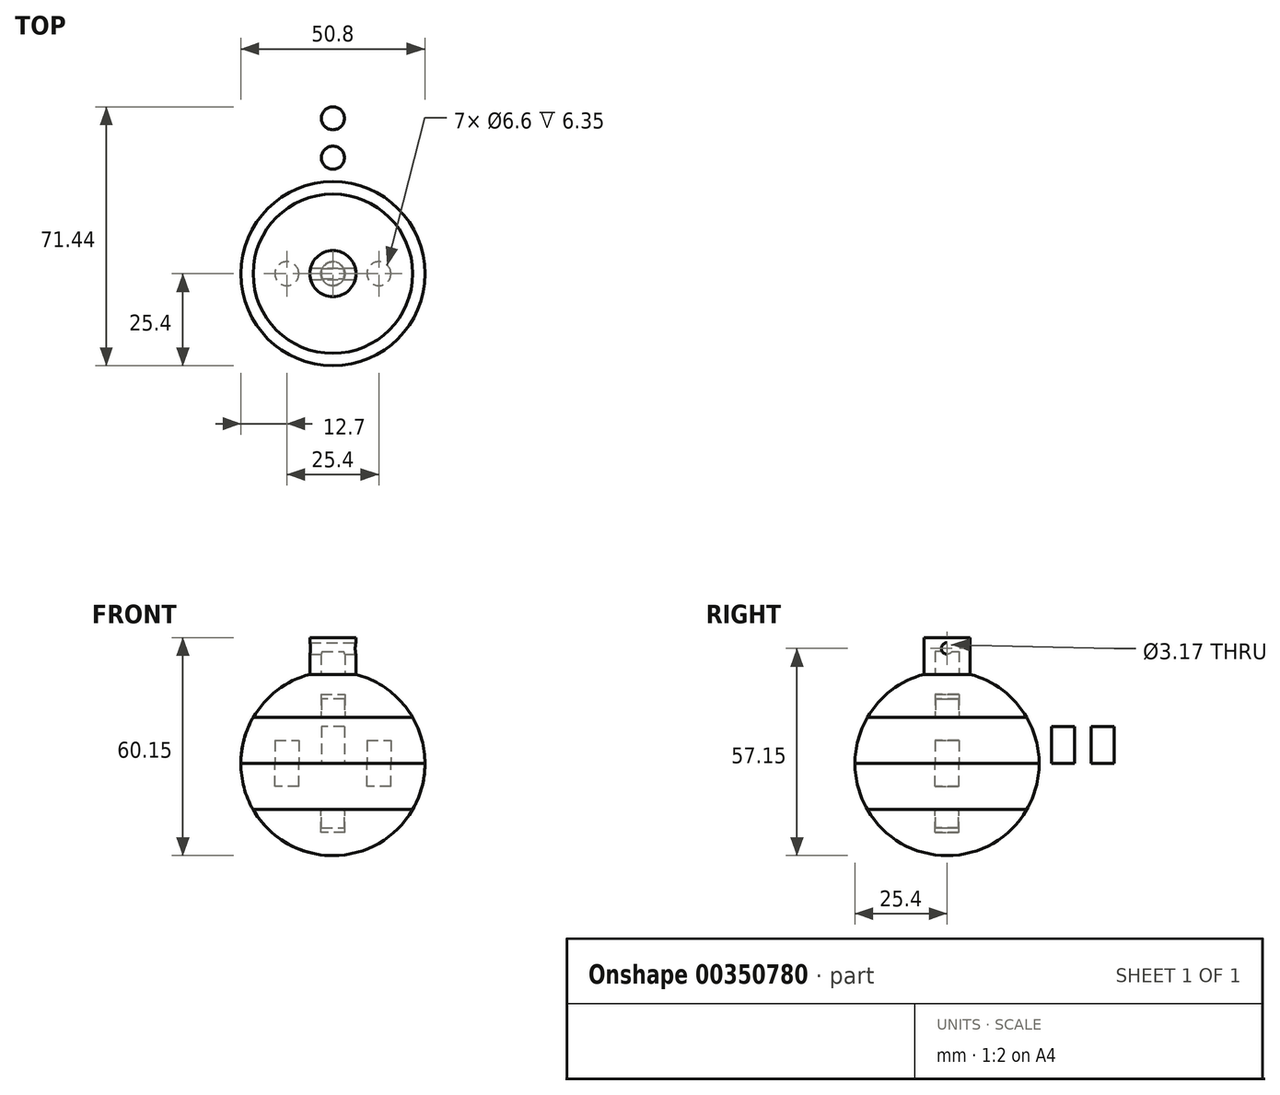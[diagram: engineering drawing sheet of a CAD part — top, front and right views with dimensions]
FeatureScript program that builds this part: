
annotation { "Feature Type Name" : "Feature", "Feature Type Description" : "" }
export const myFeature = defineFeature(function(context is Context, id is Id, definition is map)
    precondition{}
    {
        {
            var Q0;
            Q0=qCreatedBy(makeId("Front.planeOp"),FACE);
            var sketch = newSketch(context, id + "F0", { "sketchPlane" : qUnion([Q0])});
            skArc(sketch, "E0", {"start": v(0, -25.4) * mm, "mid": v(12.7, -22) * mm, "end": v(22, -12.7) * mm});
            skLineSegment(sketch, "E1", {"start": v(0, -25.4) * mm, "end": v(0, -12.7) * mm});
            skLineSegment(sketch, "E2", {"start": v(0, -12.7) * mm, "end": v(22, -12.7) * mm});
            skSolve(sketch);
        }
        {
            var Q0;
            Q0 = qSketchRegion(id + "F0", true);
            var Q1;
            Q1=sQuery(id+"F0.wireOp",EDGE,"E1");
            revolve(context, id + "F1", {"entities" : qUnion([Q0]), "axis" : qUnion([Q1]), "revolveType" : RevolveType.FULL});
        }
        {
            var Q0;
            Q0=qCreatedBy(makeId("Front.planeOp"),FACE);
            var sketch = newSketch(context, id + "F2", { "sketchPlane" : qUnion([Q0])});
            skArc(sketch, "E3", {"start": v(22, -12.7) * mm, "mid": v(24.53, -6.57) * mm, "end": v(25.4, 0) * mm});
            skLineSegment(sketch, "E4", {"start": v(0, 0) * mm, "end": v(25.4, 0) * mm});
            skLineSegment(sketch, "E5", {"start": v(0, 0) * mm, "end": v(0, -12.7) * mm});
            skLineSegment(sketch, "E6", {"start": v(0, -12.7) * mm, "end": v(22, -12.7) * mm});
            skSolve(sketch);
        }
        {
            var Q0;
            Q0 = qSketchRegion(id + "F2", true);
            var Q1;
            Q1=sQuery(id+"F2.wireOp",EDGE,"E5");
            revolve(context, id + "F3", {"entities" : qUnion([Q0]), "axis" : qUnion([Q1]), "revolveType" : RevolveType.FULL});
        }
        {
            var Q0;
            Q0=qCreatedBy(makeId("Front.planeOp"),FACE);
            var sketch = newSketch(context, id + "F4", { "sketchPlane" : qUnion([Q0])});
            skArc(sketch, "E7", {"start": v(25.4, 0) * mm, "mid": v(24.53, 6.57) * mm, "end": v(22, 12.7) * mm});
            skLineSegment(sketch, "E8", {"start": v(0, 0) * mm, "end": v(25.4, 0) * mm});
            skLineSegment(sketch, "E9", {"start": v(0, 0) * mm, "end": v(0, 12.7) * mm});
            skLineSegment(sketch, "E10", {"start": v(0, 12.7) * mm, "end": v(22, 12.7) * mm});
            skSolve(sketch);
        }
        {
            var Q0;
            Q0=makeQuery(id+"F4.imprint","IMPRINT",FACE,{"disambiguationData":[TD([[makeQuery(id+"F4.imprint","IMPRINT",EDGE,{"derivedFrom":sQuery(id+"F4.wireOp",EDGE,"E7")}),1.0]])]});
            var Q1;
            Q1=sQuery(id+"F4.wireOp",EDGE,"E9");
            revolve(context, id + "F5", {"entities" : qUnion([Q0]), "axis" : qUnion([Q1]), "revolveType" : RevolveType.FULL});
        }
        {
            var Q0;
            Q0=qCreatedBy(makeId("Front.planeOp"),FACE);
            var sketch = newSketch(context, id + "F6", { "sketchPlane" : qUnion([Q0])});
            skArc(sketch, "E11", {"start": v(22, 12.7) * mm, "mid": v(15.37, 20.22) * mm, "end": v(6.35, 24.6) * mm});
            skLineSegment(sketch, "E12", {"start": v(0, 24.6) * mm, "end": v(0, 12.7) * mm});
            skLineSegment(sketch, "E13", {"start": v(0, 12.7) * mm, "end": v(22, 12.7) * mm});
            skLineSegment(sketch, "E14", {"start": v(0, 24.6) * mm, "end": v(6.35, 24.6) * mm});
            skPoint(sketch, "E15.orphan", {"position": v(0, 25.4) * mm});
            skSolve(sketch);
        }
        {
            var Q0;
            Q0 = qSketchRegion(id + "F6", true);
            var Q1;
            Q1=sQuery(id+"F6.wireOp",EDGE,"E12");
            revolve(context, id + "F7", {"entities" : qUnion([Q0]), "axis" : qUnion([Q1]), "revolveType" : RevolveType.FULL});
        }
        {
            var Q0;
            Q0=makeQuery(id+"F7.opRevolve","SWEPT_FACE",FACE,{"disambiguationData":[OSD([sQuery(id+"F6.wireOp",EDGE,"E14")])]});
            var sketch = newSketch(context, id + "F8", { "sketchPlane" : qUnion([Q0])});
            skCircle(sketch, "E16", {"center": v(0, 0) * mm, "radius": 3.18 * mm});
            skSolve(sketch);
        }
        {
            var Q0;
            Q0=makeQuery(id+"F8.imprint","IMPRINT",FACE,{"disambiguationData":[TD([[makeQuery(id+"F8.imprint","IMPRINT",EDGE,{"derivedFrom":sQuery(id+"F8.wireOp",EDGE,"E16")}),1.0]])]});
            extrude(context, id + "F9", {"entities" : qUnion([Q0]), "operationType" : NewBodyOperationType.ADD, "depth" : 5.08 * mm});
        }
        {
            var Q0;
            Q0=makeQuery(id+"F7.opRevolve","SWEPT_FACE",FACE,{"disambiguationData":[OSD([sQuery(id+"F6.wireOp",EDGE,"E14")])]});
            var sketch = newSketch(context, id + "F10", { "sketchPlane" : qUnion([Q0])});
            skCircle(sketch, "E17", {"center": v(0, 0) * mm, "radius": 6.35 * mm});
            skSolve(sketch);
        }
        {
            var Q0;
            Q0 = qSketchRegion(id + "F10", true);
            extrude(context, id + "F11", {"entities" : qUnion([Q0]), "depth" : 10.16 * mm});
        }
        {
            var Q0;
            Q0=qCreatedBy(makeId("Right.planeOp"),FACE);
            var sketch = newSketch(context, id + "F12", { "sketchPlane" : qUnion([Q0])});
            skCircle(sketch, "E18", {"center": v(0, 31.75) * mm, "radius": 1.59 * mm});
            skSolve(sketch);
        }
        {
            var Q0;
            Q0 = qSketchRegion(id + "F12", true);
            extrude(context, id + "F13", {"entities" : qUnion([Q0]), "operationType" : NewBodyOperationType.REMOVE, "oppositeDirection" : true, "depth" : 25.4 * mm, "hasSecondDirection" : true, "secondDirectionOppositeDirection" : false, "secondDirectionDepth" : 25.4 * mm});
        }
        {
            var Q0;
            Q0=makeQuery(id+"F11.opExtrude","CAP_FACE",FACE,{"disambiguationData":[OSD([sQuery(id+"F10.wireOp",EDGE,"E17")])],"isStart":true});
            var sketch = newSketch(context, id + "F14", { "sketchPlane" : qUnion([Q0])});
            skCircle(sketch, "E19", {"center": v(0, 0) * mm, "radius": 3.3 * mm});
            skSolve(sketch);
        }
        {
            var Q0;
            Q0=makeQuery(id+"F14.imprint","IMPRINT",FACE,{"disambiguationData":[TD([[makeQuery(id+"F14.imprint","IMPRINT",EDGE,{"derivedFrom":sQuery(id+"F14.wireOp",EDGE,"E19")}),1.0]])]});
            extrude(context, id + "F15", {"entities" : qUnion([Q0]), "operationType" : NewBodyOperationType.REMOVE, "oppositeDirection" : true, "depth" : 6.35 * mm});
        }
        {
            var Q0;
            Q0=makeQuery(id+"F7.opRevolve","SWEPT_FACE",FACE,{"disambiguationData":[OSD([sQuery(id+"F6.wireOp",EDGE,"E13")])]});
            var sketch = newSketch(context, id + "F16", { "sketchPlane" : qUnion([Q0])});
            skCircle(sketch, "E20", {"center": v(0, 0) * mm, "radius": 3.3 * mm});
            skSolve(sketch);
        }
        {
            var Q0;
            Q0=makeQuery(id+"F16.imprint","IMPRINT",FACE,{"disambiguationData":[TD([[makeQuery(id+"F16.imprint","IMPRINT",EDGE,{"derivedFrom":sQuery(id+"F16.wireOp",EDGE,"E20")}),1.0]])]});
            extrude(context, id + "F17", {"entities" : qUnion([Q0]), "operationType" : NewBodyOperationType.REMOVE, "oppositeDirection" : true, "depth" : 6.35 * mm});
        }
        {
            var Q0;
            Q0=makeQuery(id+"F1.opRevolve","SWEPT_FACE",FACE,{"disambiguationData":[OSD([sQuery(id+"F0.wireOp",EDGE,"E2")])]});
            var sketch = newSketch(context, id + "F18", { "sketchPlane" : qUnion([Q0])});
            skCircle(sketch, "E21", {"center": v(0, 0) * mm, "radius": 3.3 * mm});
            skSolve(sketch);
        }
        {
            var Q0;
            Q0 = qSketchRegion(id + "F18", true);
            extrude(context, id + "F19", {"entities" : qUnion([Q0]), "operationType" : NewBodyOperationType.REMOVE, "oppositeDirection" : true, "depth" : 6.35 * mm});
        }
        {
            var Q0;
            Q0=makeQuery(id+"F5.opRevolve","SWEPT_FACE",FACE,{"disambiguationData":[OSD([sQuery(id+"F4.wireOp",EDGE,"E10")])]});
            var sketch = newSketch(context, id + "F20", { "sketchPlane" : qUnion([Q0])});
            skCircle(sketch, "E22", {"center": v(0, 0) * mm, "radius": 3.18 * mm});
            skSolve(sketch);
        }
        {
            var Q0;
            Q0 = qSketchRegion(id + "F20", true);
            extrude(context, id + "F21", {"entities" : qUnion([Q0]), "operationType" : NewBodyOperationType.ADD, "depth" : 5.08 * mm});
        }
        {
            var Q0;
            Q0=makeQuery(id+"F3.opRevolve","SWEPT_FACE",FACE,{"disambiguationData":[OSD([sQuery(id+"F2.wireOp",EDGE,"E6")])]});
            var sketch = newSketch(context, id + "F22", { "sketchPlane" : qUnion([Q0])});
            skCircle(sketch, "E23", {"center": v(0, 0) * mm, "radius": 3.18 * mm});
            skSolve(sketch);
        }
        {
            var Q0;
            Q0 = qSketchRegion(id + "F22", true);
            extrude(context, id + "F23", {"entities" : qUnion([Q0]), "operationType" : NewBodyOperationType.ADD, "depth" : 5.08 * mm});
        }
        {
            var Q0;
            Q0=makeQuery(id+"F3.opRevolve","SWEPT_FACE",FACE,{"disambiguationData":[OSD([sQuery(id+"F2.wireOp",EDGE,"E4")])]});
            var sketch = newSketch(context, id + "F24", { "sketchPlane" : qUnion([Q0])});
            skCircle(sketch, "E24", {"center": v(12.7, 0) * mm, "radius": 3.3 * mm});
            skCircle(sketch, "E25", {"center": v(-12.7, 0) * mm, "radius": 3.3 * mm});
            skSolve(sketch);
        }
        {
            var Q0;
            Q0 = qSketchRegion(id + "F24", true);
            extrude(context, id + "F25", {"entities" : qUnion([Q0]), "operationType" : NewBodyOperationType.REMOVE, "oppositeDirection" : true, "depth" : 6.35 * mm});
        }
        {
            var Q0;
            Q0=qCreatedBy(makeId("Top.planeOp"),FACE);
            var sketch = newSketch(context, id + "F26", { "sketchPlane" : qUnion([Q0])});
            skCircle(sketch, "E26", {"center": v(0, 31.98) * mm, "radius": 3.18 * mm});
            skCircle(sketch, "E27", {"center": v(0, 42.87) * mm, "radius": 3.18 * mm});
            skSolve(sketch);
        }
        {
            var Q0;
            Q0 = qSketchRegion(id + "F26", true);
            extrude(context, id + "F27", {"entities" : qUnion([Q0]), "depth" : 10.16 * mm});
        }
        {
            var Q0;
            Q0=makeQuery(id+"F5.opRevolve","SWEPT_FACE",FACE,{"disambiguationData":[OSD([sQuery(id+"F4.wireOp",EDGE,"E8")])]});
            var sketch = newSketch(context, id + "F28", { "sketchPlane" : qUnion([Q0])});
            skCircle(sketch, "E28", {"center": v(-12.7, 0) * mm, "radius": 3.3 * mm});
            skCircle(sketch, "E29", {"center": v(12.7, 0) * mm, "radius": 3.3 * mm});
            skPoint(sketch, "E30", {"position": v(0, 0) * mm});
            skSolve(sketch);
        }
        {
            var Q0;
            Q0 = qSketchRegion(id + "F28", true);
            extrude(context, id + "F29", {"entities" : qUnion([Q0]), "operationType" : NewBodyOperationType.REMOVE, "oppositeDirection" : true, "depth" : 6.35 * mm});
        }
    });
